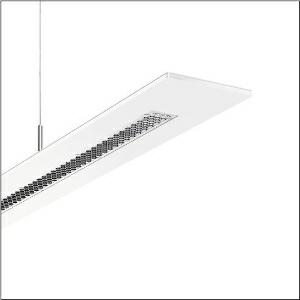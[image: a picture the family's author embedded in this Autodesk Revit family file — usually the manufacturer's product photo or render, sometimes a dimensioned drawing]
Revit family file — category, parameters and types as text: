
# Revit family: arktika_r__21_duo_5mb252dl60830_d82e
name_source: partatom
category: Lighting Fixtures
units: mm (PartAtom-declared; Revit-internal decimal feet)

## family parameters
Cut with Voids When Loaded = No
Host = Face
Light Source = No
Part Type = Normal
Room Calculation Point = No
Round Connector Dimension = Use Diameter
Shared = No

## types (1)
- --- (1 x LED 3000K / CRI = 80 (unbekannt), 8100 lm, 3000K)
    Apparent Load = 67 VA
    CIE Flux Codes = 81 100 100 79 100
    Color Rendering = 80
    Color Temperature = 3000K
    Default Elevation = 1800 mm
    Description = Arktika® 21 duo, office luminaire, primary anti-glare with honeycomb louvre, of plastic, aluminium vaporised, highly specular, light emission: direct/indirect distribution, primary light characteristic: symmetric, installation type: suspended mounting, LED, rated luminous flux: 8.100lm, luminous efficacy: 122lm/W, light colour: 830, colour temperature: 3000K, control gear: DALI, with terminal, 3+2-pole, max. 2.5mm², mains connection: 220..240V, AC, 50/60Hz, rated input power: 67W, housing, of aluminium, powder-coated, traffic white (RAL 9016), 2-length, length: 2.280mm, width: 120mm, height: 8mm, protection rating (complete): IP20, insulation class (complete): insulation class II (safety insulation), certification: CE, packaging unit: 1 piece
    Height = 8 mm  [stored 0.0262467 ft]
    Lamp = 1 x LED 3000K / CRI >= 80 (unbekannt)
    Lamp Light Flux = 8100 lm
    Lamp count = 1
    Length = 2280 mm
    Luminous efficacy = 122 lm/W
    Manufacturer = Siteco
    ModVariant = No
    Model = 5MB252DL60830
    Mounting Place = Ceiling
    Mounting Type = Pendant
    Number of Poles = 1
    OnlyDefault = Yes
    Power Factor = 1
    Product Name = Arktika® 21 duo
    Product group = office luminaire | ceiling pendant
    ProductGroupID = 904
    Protection Class = Protection class II
    Protection Degree = IP 20
    RLX_Detail_Level = 1
    RLX_Emergency_Light_Flux = 0 lm
    RLX_Emergency_Type = 0
    RLX_Emergency_Type_DB = No
    RlxData = <blob elided: 39773 chars, md5=a3367783>
    Socket = socket
    Standby Power = 0 W
    System Light Flux = 8100 lm
    System Power = 67 W
    Type Comments = factory setting: luminous flux: 100 % | dim-lin: 254 | 1330 mA
    Type Image = l_1006128.jpg
    URL = http://relux.com
    VarID = @adj_202916
    Voltage = 0 V
    Weight = 0.00 kg
    Width = 120 mm

note: [stored X ft] marks values corroborated as IEEE doubles in the binary element streams (Revit-internal decimal feet)

## geometry (parser evidence)
native form markers: Blend x4, Sweep x13
no freeform markers — native parametric forms only
